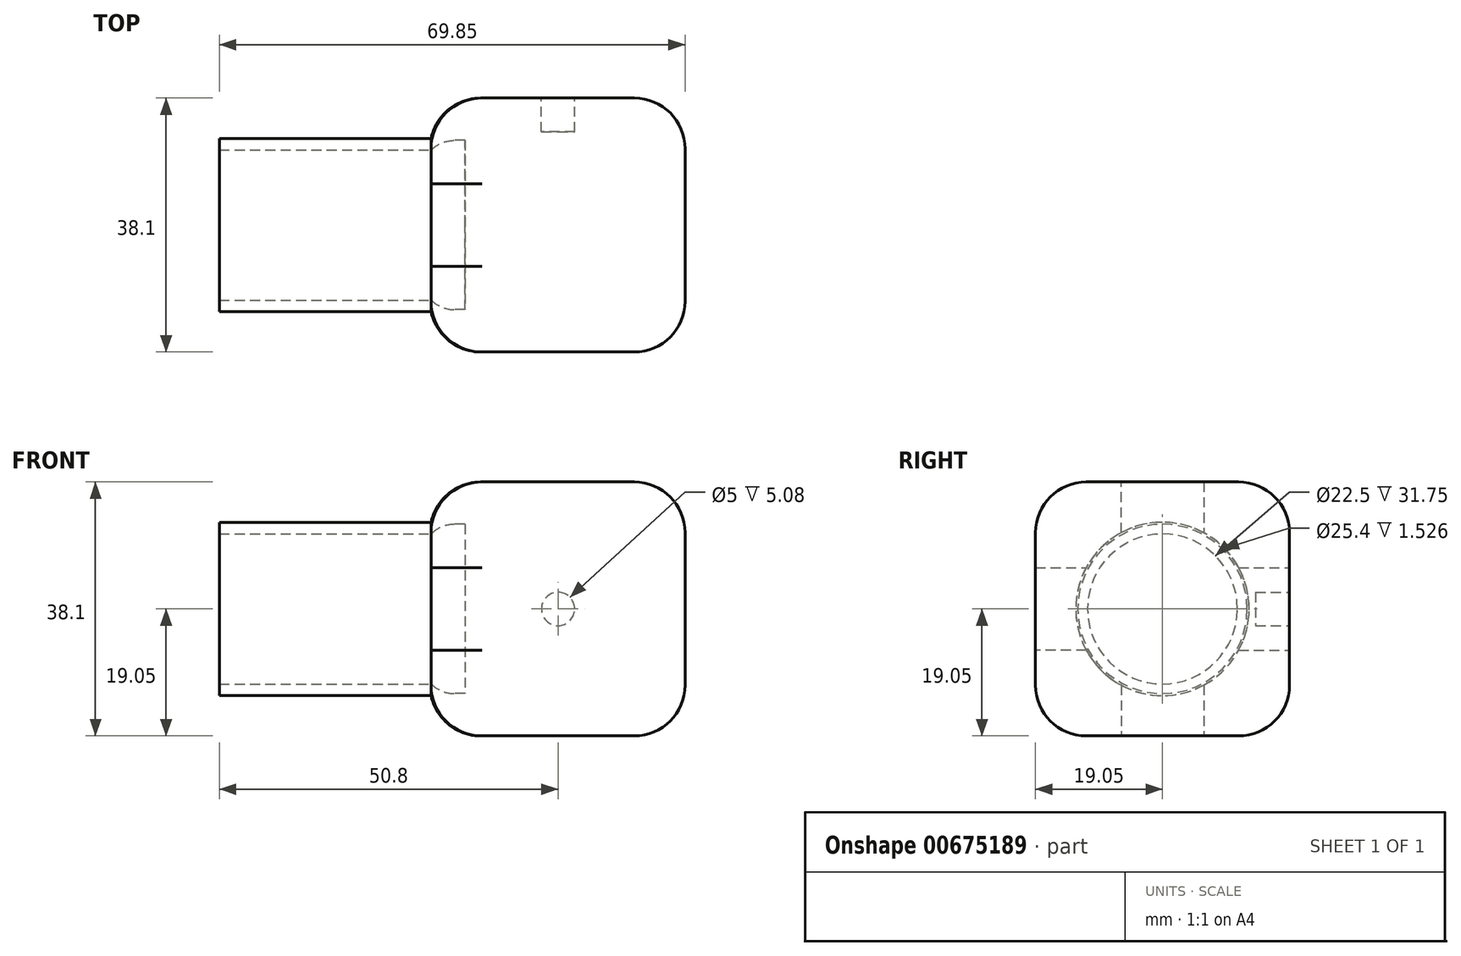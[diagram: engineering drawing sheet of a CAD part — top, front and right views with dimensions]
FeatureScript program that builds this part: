
annotation { "Feature Type Name" : "Feature", "Feature Type Description" : "" }
export const myFeature = defineFeature(function(context is Context, id is Id, definition is map)
    precondition{}
    {
        {
            var Q0;
            Q0=qCreatedBy(makeId("Right.planeOp"),FACE);
            var sketch = newSketch(context, id + "F0", { "sketchPlane" : qUnion([Q0])});
            skLineSegment(sketch, "E0.bottom", {"start": v(0, 0) * mm, "end": v(38.1, 0) * mm});
            skLineSegment(sketch, "E0.top", {"start": v(0, -38.1) * mm, "end": v(38.1, -38.1) * mm});
            skLineSegment(sketch, "E0.left", {"start": v(0, 0) * mm, "end": v(0, -38.1) * mm});
            skLineSegment(sketch, "E0.right", {"start": v(38.1, 0) * mm, "end": v(38.1, -38.1) * mm});
            skSolve(sketch);
        }
        {
            var Q0;
            Q0=qSketchRegion(id+"F0",true);
            extrude(context, id + "F1", {"entities" : qUnion([Q0]), "depth" : 38.1 * mm, "offsetDistance" : 25.4 * mm});
        }
        {
            var Q0;
            Q0=makeQuery(id+"F1.opExtrude","SWEPT_FACE",FACE,{"disambiguationData":[OSD([sQuery(id+"F0.wireOp",EDGE,"E0.right")])]});
            var sketch = newSketch(context, id + "F2", { "sketchPlane" : qUnion([Q0])});
            skCircle(sketch, "E1", {"center": v(-19.05, -19.05) * mm, "radius": 11.25 * mm});
            skPoint(sketch, "E1.centerSnap0", {"position": v(-38.1, -19.05) * mm});
            skPoint(sketch, "E1.centerSnap1", {"position": v(-19.05, 0) * mm});
            skCircle(sketch, "E2", {"center": v(-19.05, -19.05) * mm, "radius": 13 * mm});
            skSolve(sketch);
        }
        {
            var Q0;
            Q0=makeQuery(id+"F1.opExtrude","CAP_FACE",FACE,{"disambiguationData":[OSD([sQuery(id+"F0.wireOp",EDGE,"E0.bottom"),sQuery(id+"F0.wireOp",EDGE,"E0.top"),sQuery(id+"F0.wireOp",EDGE,"E0.left"),sQuery(id+"F0.wireOp",EDGE,"E0.right")])],"isStart":true});
            var sketch = newSketch(context, id + "F3", { "sketchPlane" : qUnion([Q0])});
            skCircle(sketch, "E3", {"center": v(-19.05, -19.05) * mm, "radius": 11.25 * mm});
            skPoint(sketch, "E3.centerSnap0", {"position": v(-19.05, 0) * mm});
            skPoint(sketch, "E3.centerSnap1", {"position": v(-38.1, -19.05) * mm});
            skCircle(sketch, "E4", {"center": v(-19.05, -19.05) * mm, "radius": 13 * mm});
            skSolve(sketch);
        }
        {
            var Q0;
            Q0=qSketchRegion(id+"F3",true);
            extrude(context, id + "F4", {"entities" : qUnion([Q0]), "operationType" : NewBodyOperationType.ADD, "depth" : 31.75 * mm, "offsetDistance" : 25.4 * mm});
        }
        {
            var Q0;
            Q0=makeQuery(id+"F1.opExtrude","CAP_EDGE",EDGE,{"disambiguationData":[OSD([sQuery(id+"F0.wireOp",EDGE,"E0.right")])],"isStart":true});
            var Q1;
            Q1=makeQuery(id+"F1.opExtrude","SWEPT_FACE",FACE,{"disambiguationData":[OSD([sQuery(id+"F0.wireOp",EDGE,"E0.bottom")])]});
            var Q2;
            Q2=makeQuery(id+"F1.opExtrude","CAP_EDGE",EDGE,{"disambiguationData":[OSD([sQuery(id+"F0.wireOp",EDGE,"E0.left")])],"isStart":true});
            var Q3;
            Q3=makeQuery(id+"F1.opExtrude","CAP_EDGE",EDGE,{"disambiguationData":[OSD([sQuery(id+"F0.wireOp",EDGE,"E0.left")])],"isStart":false});
            var Q4;
            Q4=makeQuery(id+"F1.opExtrude","CAP_EDGE",EDGE,{"disambiguationData":[OSD([sQuery(id+"F0.wireOp",EDGE,"E0.right")])],"isStart":false});
            var Q5;
            Q5=makeQuery(id+"F1.opExtrude","SWEPT_EDGE",EDGE,{"disambiguationData":[OSD([sQuery(id+"F0.wireOp",EDGE,"E0.top"),sQuery(id+"F0.wireOp",EDGE,"E0.right")])]});
            var Q6;
            Q6=makeQuery(id+"F1.opExtrude","CAP_EDGE",EDGE,{"disambiguationData":[OSD([sQuery(id+"F0.wireOp",EDGE,"E0.top")])],"isStart":false});
            var Q7;
            Q7=makeQuery(id+"F1.opExtrude","CAP_EDGE",EDGE,{"disambiguationData":[OSD([sQuery(id+"F0.wireOp",EDGE,"E0.top")])],"isStart":true});
            var Q8;
            Q8=makeQuery(id+"F1.opExtrude","SWEPT_EDGE",EDGE,{"disambiguationData":[OSD([sQuery(id+"F0.wireOp",EDGE,"E0.top"),sQuery(id+"F0.wireOp",EDGE,"E0.left")])]});
            fillet(context, id + "F5", {"entities" : qUnion([Q0, Q1, Q2, Q3, Q4, Q5, Q6, Q7, Q8]), "radius" : 7.62 * mm, "tangentPropagation" : true, "allowEdgeOverflow" : false});
        }
        {
            var Q0;
            Q0=makeQuery(id+"F4.boolean.opBoolean","SPLIT",FACE,{"disambiguationData":[TD([makeQuery(id+"F4.opExtrude","SWEPT_FACE",FACE,{"disambiguationData":[OSD([sQuery(id+"F3.wireOp",EDGE,"E3")])]})])],"derivedFrom":makeQuery(id+"F1.opExtrude","CAP_FACE",FACE,{"disambiguationData":[OSD([sQuery(id+"F0.wireOp",EDGE,"E0.bottom"),sQuery(id+"F0.wireOp",EDGE,"E0.top"),sQuery(id+"F0.wireOp",EDGE,"E0.left"),sQuery(id+"F0.wireOp",EDGE,"E0.right")])],"isStart":true})});
            var sketch = newSketch(context, id + "F6", { "sketchPlane" : qUnion([Q0])});
            skCircle(sketch, "E5", {"center": v(-19.05, -19.05) * mm, "radius": 12.7 * mm});
            skSolve(sketch);
        }
        {
            var Q0;
            Q0=qSketchRegion(id+"F6",true);
            extrude(context, id + "F7", {"entities" : qUnion([Q0]), "operationType" : NewBodyOperationType.REMOVE, "oppositeDirection" : true, "depth" : 5.08 * mm, "offsetDistance" : 25.4 * mm});
        }
        {
            var Q0;
            Q0=makeQuery(id+"F7.boolean.opBoolean","COPY",EDGE,{"derivedFrom":makeQuery(id+"F7.opExtrude","CAP_EDGE",EDGE,{"disambiguationData":[OSD([sQuery(id+"F6.wireOp",EDGE,"E5")])],"isStart":true})});
            fillet(context, id + "F8", {"entities" : qUnion([Q0]), "radius" : 5.08 * mm, "tangentPropagation" : true, "allowEdgeOverflow" : false});
        }
        {
            var Q0;
            Q0=makeQuery(id+"Fc77rQdDxEQxCS8_1.boolean.opBoolean","SPLIT",FACE,{"disambiguationData":[TD([makeQuery(id+"Fc77rQdDxEQxCS8_1.opExtrude","SWEPT_FACE",FACE,{"disambiguationData":[OSD([sQuery(id+"F2.wireOp",EDGE,"E1")])]})])],"derivedFrom":makeQuery(id+"F1.opExtrude","SWEPT_FACE",FACE,{"disambiguationData":[OSD([sQuery(id+"F0.wireOp",EDGE,"E0.right")])]})});
            var sketch = newSketch(context, id + "F9", { "sketchPlane" : qUnion([Q0])});
            skCircle(sketch, "E6", {"center": v(-19.05, -19.05) * mm, "radius": 2.5 * mm});
            skSolve(sketch);
        }
        {
            var Q0;
            Q0=makeQuery(id+"F9.imprint","IMPRINT",FACE,{"disambiguationData":[TD([[makeQuery(id+"F9.imprint","IMPRINT",EDGE,{"derivedFrom":sQuery(id+"F9.wireOp",EDGE,"E6")}),1.0]])]});
            extrude(context, id + "F10", {"entities" : qUnion([Q0]), "operationType" : NewBodyOperationType.REMOVE, "oppositeDirection" : true, "depth" : 5.08 * mm, "offsetDistance" : 25.4 * mm});
        }
    });
